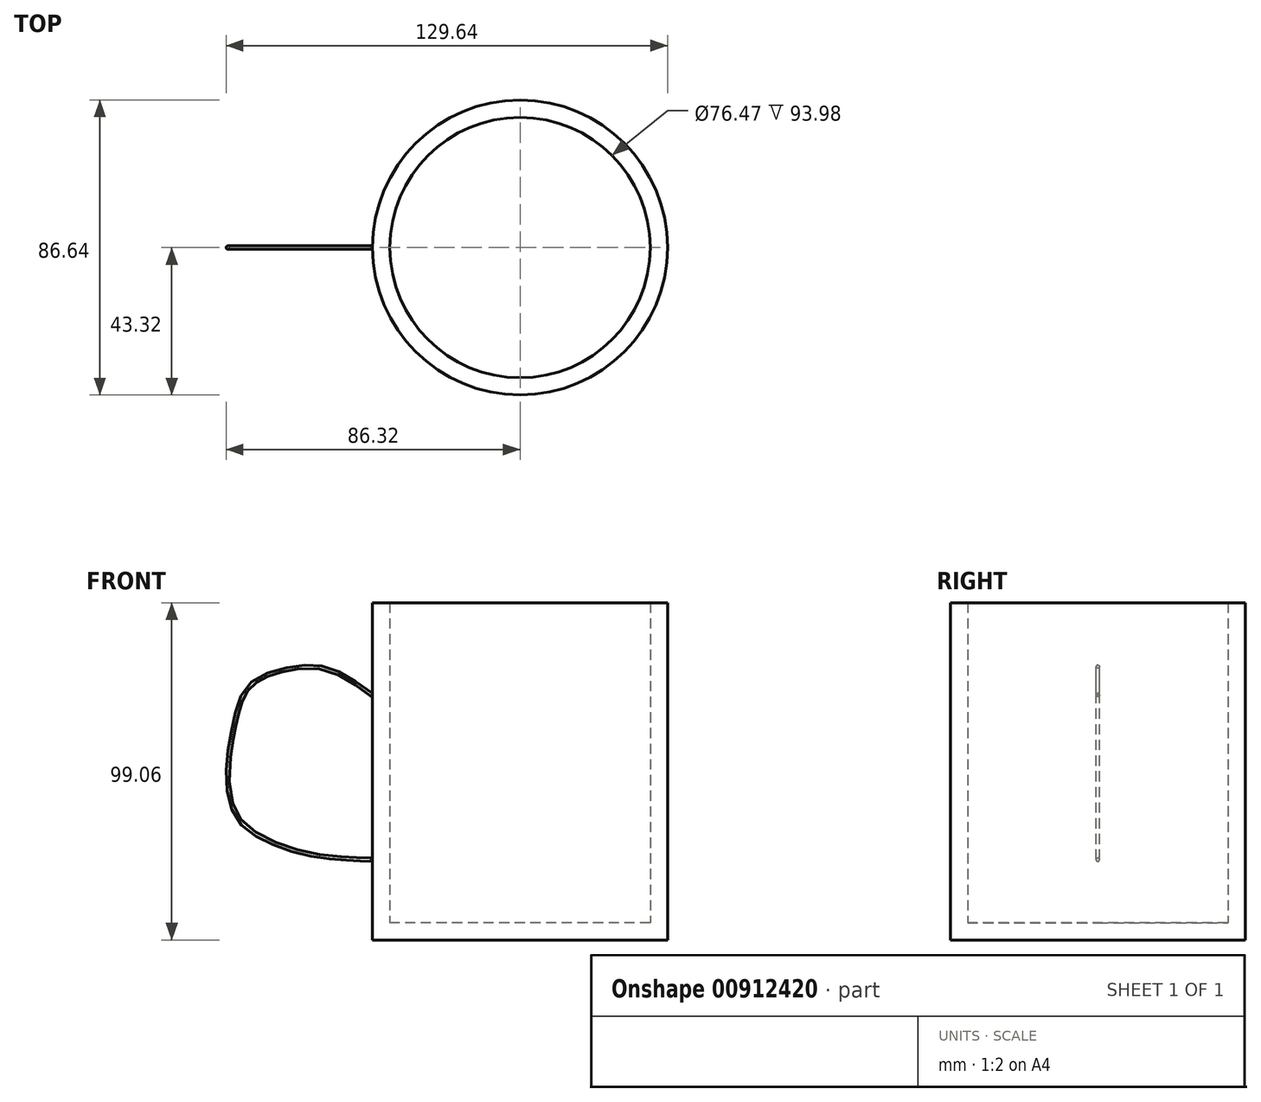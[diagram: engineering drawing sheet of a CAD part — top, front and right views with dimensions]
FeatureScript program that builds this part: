
annotation { "Feature Type Name" : "Feature", "Feature Type Description" : "" }
export const myFeature = defineFeature(function(context is Context, id is Id, definition is map)
    precondition{}
    {
        {
            var Q0;
            Q0=qCreatedBy(makeId("Top.planeOp"),FACE);
            var sketch = newSketch(context, id + "F0", { "sketchPlane" : qUnion([Q0])});
            skCircle(sketch, "E0", {"center": v(0, 0) * mm, "radius": 43.32 * mm});
            skSolve(sketch);
        }
        {
            var Q0;
            Q0 = qSketchRegion(id + "F0", true);
            extrude(context, id + "F1", {"entities" : qUnion([Q0]), "depth" : 99.06 * mm, "offsetDistance" : 25.4 * mm});
        }
        {
            var Q0;
            Q0=makeQuery(id+"F1.opExtrude","CAP_FACE",FACE,{"disambiguationData":[OSD([sQuery(id+"F0.wireOp",EDGE,"E0")])],"isStart":false});
            var Q1;
            Q1=makeQuery(id+"F1.opExtrude","SWEPT_BODY",BODY,{"disambiguationData":[OSD([sQuery(id+"F0.wireOp",EDGE,"E0")])]});
            shell(context, id + "F2", {"entities" : qUnion([Q0]), "parts" : qUnion([Q1]), "thickness" : 5.08 * mm});
        }
        {
            var Q0;
            Q0=qCreatedBy(makeId("Front.planeOp"),FACE);
            var sketch = newSketch(context, id + "F3", { "sketchPlane" : qUnion([Q0])});
            skFitSpline(sketch, "E1", {"points": [v(-43.32, 71.9) * mm, v(-55.8, 79.37) * mm, v(-66.83, 79.87) * mm, v(-79.09, 74.97) * mm, v(-83.64, 64.7) * mm, v(-85.83, 50.46) * mm, v(-83.4, 36.58) * mm, v(-73.82, 29.01) * mm, v(-59.93, 24.74) * mm, v(-48.97, 23.76) * mm, v(-43.69, 23.54) * mm], "startDerivative": vector(-114.2, 82.87) * mm, "endDerivative": vector(72.61, -3.03) * mm});
            skSolve(sketch);
        }
        {
            var Q0;
            Q0=sQuery(id+"F3.wireOp",VERTEX,"E1.start");
            var Q1;
            Q1=sQuery(id+"F3.wireOp",EDGE,"E1");
            cPlane(context, id + "F4", {"entities" : qUnion([Q0, Q1]), "cplaneType" : CPlaneType.CURVE_POINT, "offset" : 25.4 * mm, "width" : 152.4 * mm, "height" : 152.4 * mm});
        }
        {
            var Q0;
            Q0=qCreatedBy(id+"F4.planeOp",FACE);
            var sketch = newSketch(context, id + "F5", { "sketchPlane" : qUnion([Q0])});
            skCircle(sketch, "E2", {"center": v(0, 32.72) * mm, "radius": 0.47 * mm});
            skSolve(sketch);
        }
        {
            var Q0;
            Q0=makeQuery(id+"F5.imprint","IMPRINT",FACE,{"disambiguationData":[TD([[makeQuery(id+"F5.imprint","IMPRINT",EDGE,{"derivedFrom":sQuery(id+"F5.wireOp",EDGE,"E2")}),1.0]])]});
            var Q1;
            Q1=sQuery(id+"F3.wireOp",EDGE,"E1");
            sweep(context, id + "F6", {"operationType" : NewBodyOperationType.ADD, "profiles" : qUnion([Q0]), "path" : qUnion([Q1])});
        }
    });
